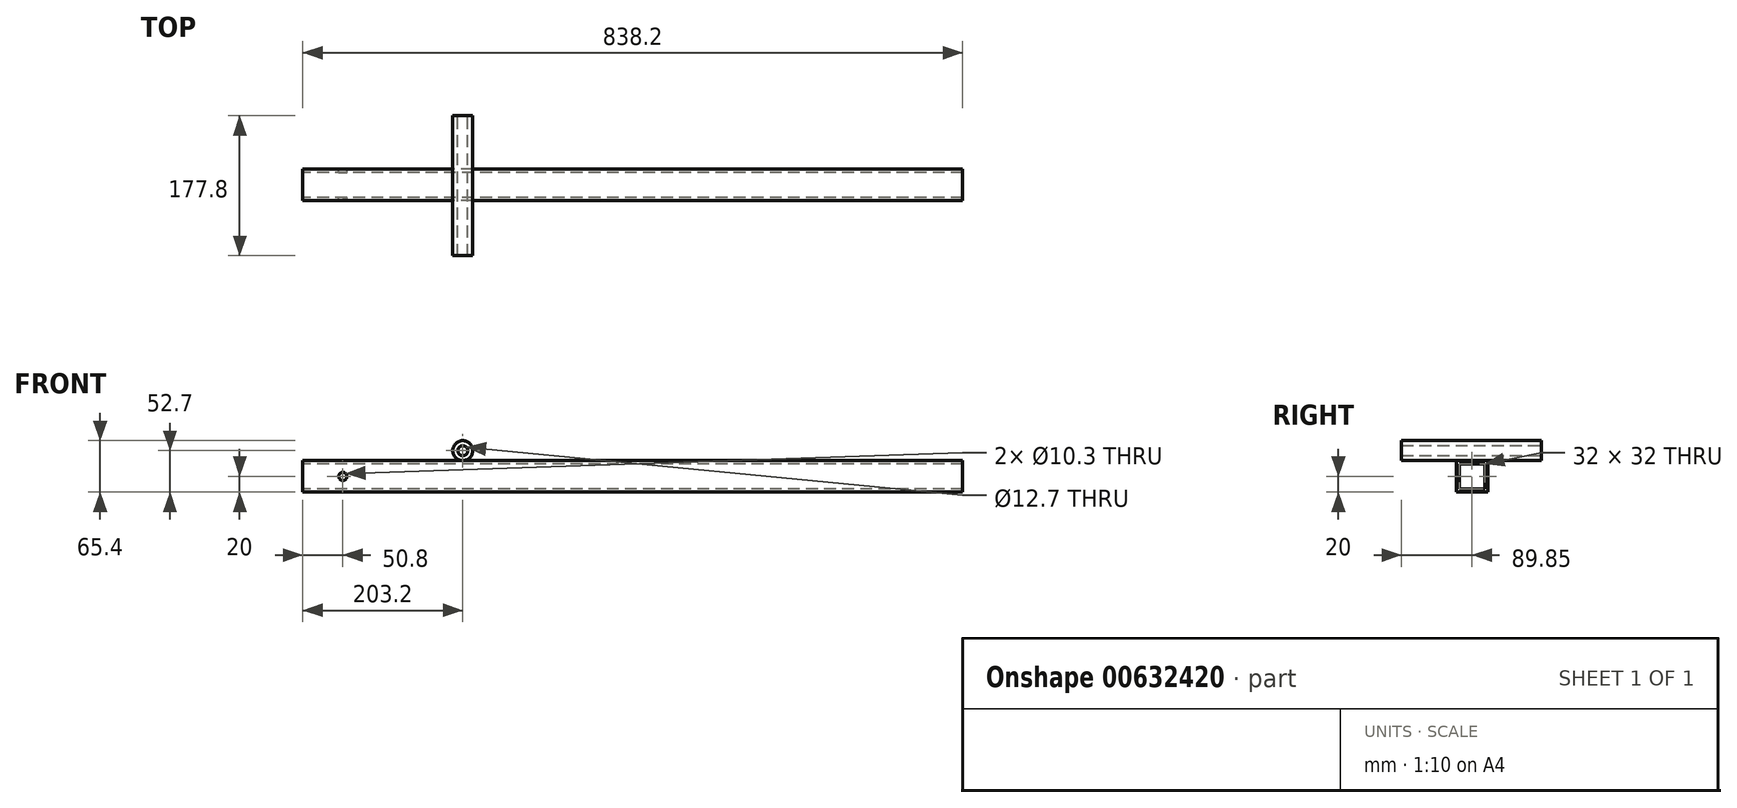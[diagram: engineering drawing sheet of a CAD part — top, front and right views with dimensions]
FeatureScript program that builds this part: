
annotation { "Feature Type Name" : "Feature", "Feature Type Description" : "" }
export const myFeature = defineFeature(function(context is Context, id is Id, definition is map)
    precondition{}
    {
        {
            var Q0;
            Q0=qCreatedBy(makeId("Right.planeOp"),FACE);
            var sketch = newSketch(context, id + "F0", { "sketchPlane" : qUnion([Q0])});
            skLineSegment(sketch, "E0.bottom", {"start": v(0, 0) * mm, "end": v(40, 0) * mm});
            skLineSegment(sketch, "E0.top", {"start": v(0, 40) * mm, "end": v(40, 40) * mm});
            skLineSegment(sketch, "E0.left", {"start": v(0, 0) * mm, "end": v(0, 40) * mm});
            skLineSegment(sketch, "E0.right", {"start": v(40, 0) * mm, "end": v(40, 40) * mm});
            skLineSegment(sketch, "E1.0", {"start": v(4, 36) * mm, "end": v(36, 36) * mm});
            skLineSegment(sketch, "E1.1", {"start": v(4, 4) * mm, "end": v(4, 36) * mm});
            skLineSegment(sketch, "E1.2", {"start": v(4, 4) * mm, "end": v(36, 4) * mm});
            skLineSegment(sketch, "E1.3", {"start": v(36, 4) * mm, "end": v(36, 36) * mm});
            skSolve(sketch);
        }
        {
            var Q0;
            Q0=makeQuery(id+"F0.imprint","IMPRINT",FACE,{"disambiguationData":[TD([[makeQuery(id+"F0.imprint","IMPRINT",EDGE,{"derivedFrom":sQuery(id+"F0.wireOp",EDGE,"E0.bottom")}),1.0]])]});
            extrude(context, id + "F1", {"entities" : qUnion([Q0]), "depth" : 838.2 * mm, "offsetDistance" : 25 * mm});
        }
        {
            var Q0;
            Q0=makeQuery(id+"F1.opExtrude","SWEPT_FACE",FACE,{"disambiguationData":[OSD([sQuery(id+"F0.wireOp",EDGE,"E0.left")])]});
            cPlane(context, id + "F2", {"entities" : qUnion([Q0]), "cplaneType" : CPlaneType.OFFSET, "offset" : 19.05 * mm, "oppositeDirection" : true, "width" : 150 * mm, "height" : 150 * mm});
        }
        {
            var Q0;
            Q0=makeQuery(id+"F1.opExtrude","SWEPT_FACE",FACE,{"disambiguationData":[OSD([sQuery(id+"F0.wireOp",EDGE,"E0.left")])]});
            var sketch = newSketch(context, id + "F3", { "sketchPlane" : qUnion([Q0])});
            skPoint(sketch, "E2", {"position": v(50.8, 20) * mm});
            skPoint(sketch, "E2.positionSnap0", {"position": v(0, 20) * mm});
            skSolve(sketch);
        }
        {
            var Q0;
            Q0=sQuery(id+"F3.wireOp",VERTEX,"E2");
            var Q1;
            Q1=makeQuery(id+"F1.opExtrude","SWEPT_BODY",BODY,{"disambiguationData":[OSD([sQuery(id+"F0.wireOp",EDGE,"E0.bottom"),sQuery(id+"F0.wireOp",EDGE,"E0.top"),sQuery(id+"F0.wireOp",EDGE,"E0.left"),sQuery(id+"F0.wireOp",EDGE,"E0.right"),sQuery(id+"F0.wireOp",EDGE,"E1.0"),sQuery(id+"F0.wireOp",EDGE,"E1.1"),sQuery(id+"F0.wireOp",EDGE,"E1.2"),sQuery(id+"F0.wireOp",EDGE,"E1.3")])]});
            hole(context, id + "F4", {"style" : HoleStyle.SIMPLE, "endStyle" : HoleEndStyle.THROUGH, "standardTappedOrClearance" : lookupTablePath({ "standard" : "ISO", "engagement" : "75%", "pitch" : "1.75 mm", "size" : "M12", "type" : "Tapped" }), "standardBlindInLast" : lookupTablePath({ "standard" : "ISO", "engagement" : "75%", "pitch" : "1.75 mm", "size" : "M12", "type" : "Tapped" }), "holeDiameter" : 10.3 * mm, "majorDiameter" : 12 * mm, "showTappedDepth" : true, "isTappedThrough" : true, "tappedDepth" : 12 * mm, "tapClearance" : 3, "startFromSketch" : true, "locations" : qUnion([Q0]), "scope" : qUnion([Q1])});
        }
        {
            var Q0;
            Q0=qCreatedBy(id+"F2.planeOp",FACE);
            var sketch = newSketch(context, id + "F5", { "sketchPlane" : qUnion([Q0])});
            skPoint(sketch, "E3.positionSnap0", {"position": v(0, 20) * mm});
            skCircle(sketch, "E4", {"center": v(203.2, 52.7) * mm, "radius": 12.7 * mm});
            skCircle(sketch, "E5.0", {"center": v(203.2, 52.7) * mm, "radius": 6.35 * mm});
            skSolve(sketch);
        }
        {
            var Q0;
            Q0=makeQuery(id+"F5.imprint","IMPRINT",FACE,{"disambiguationData":[TD([[makeQuery(id+"F5.imprint","IMPRINT",EDGE,{"derivedFrom":sQuery(id+"F5.wireOp",EDGE,"E4")}),1.0]])]});
            extrude(context, id + "F6", {"entities" : qUnion([Q0]), "operationType" : NewBodyOperationType.ADD, "depth" : 177.8 * mm, "offsetDistance" : 25 * mm, "symmetric" : true});
        }
    });
